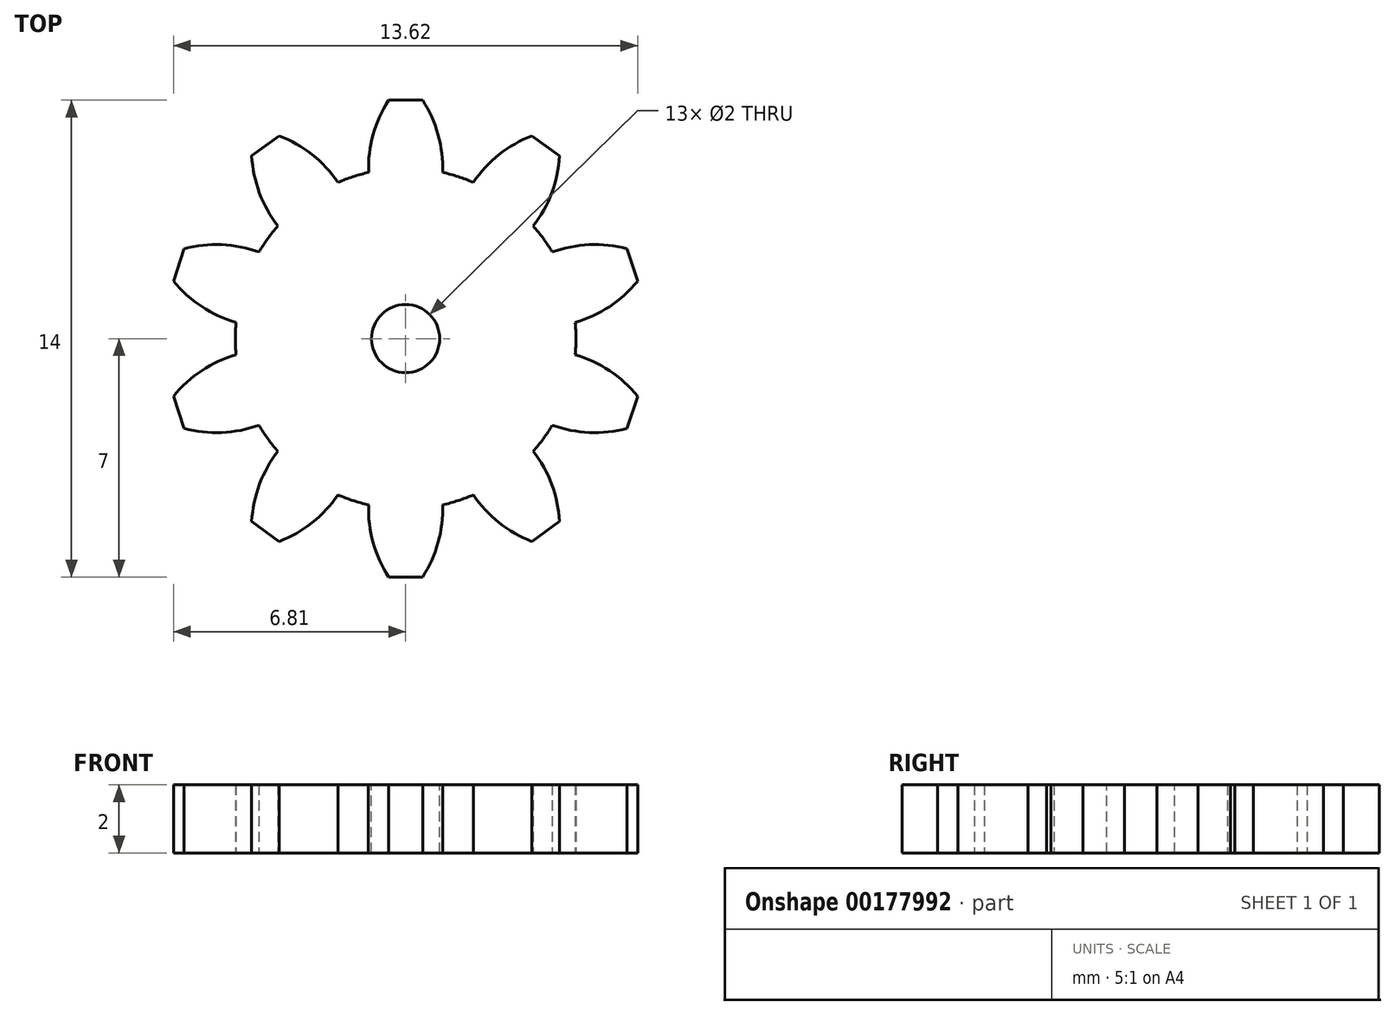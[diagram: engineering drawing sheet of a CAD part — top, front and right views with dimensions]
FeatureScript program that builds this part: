
annotation { "Feature Type Name" : "Feature", "Feature Type Description" : "" }
export const myFeature = defineFeature(function(context is Context, id is Id, definition is map)
    precondition{}
    {
        {
            var Q0;
            Q0=qCreatedBy(makeId("Top.planeOp"),FACE);
            var sketch = newSketch(context, id + "F0", { "sketchPlane" : qUnion([Q0])});
            skCircle(sketch, "E0", {"center": v(0, 0) * mm, "radius": 5 * mm});
            skLineSegment(sketch, "E1", {"start": v(0, 0) * mm, "end": v(0, 5) * mm, "construction": true});
            skLineSegment(sketch, "E2", {"start": v(0, 5) * mm, "end": v(0, 7) * mm, "construction": true});
            skLineSegment(sketch, "E3", {"start": v(0, 7) * mm, "end": v(-0.5, 7) * mm});
            skArc(sketch, "E4", {"start": v(-0.5, 7) * mm, "mid": v(-0.96, 5.98) * mm, "end": v(-1.09, 4.88) * mm});
            skLineSegment(sketch, "E5.MirrorCS", {"start": v(0, 7) * mm, "end": v(0.5, 7) * mm});
            skArc(sketch, "E6.MirrorCS", {"start": v(0.5, 7) * mm, "mid": v(0.96, 5.98) * mm, "end": v(1.09, 4.88) * mm});
            skArc(sketch, "E7.1.0", {"start": v(-4.52, 5.37) * mm, "mid": v(-4.3, 4.28) * mm, "end": v(-3.75, 3.3) * mm});
            skLineSegment(sketch, "E7.1.1", {"start": v(-4.11, 5.66) * mm, "end": v(-4.52, 5.37) * mm});
            skLineSegment(sketch, "E7.1.2", {"start": v(-4.11, 5.66) * mm, "end": v(-3.7, 5.96) * mm});
            skArc(sketch, "E7.1.3", {"start": v(-3.7, 5.96) * mm, "mid": v(-2.75, 5.4) * mm, "end": v(-1.99, 4.59) * mm});
            skArc(sketch, "E7.2.0", {"start": v(-6.81, 1.69) * mm, "mid": v(-5.99, 0.94) * mm, "end": v(-4.98, 0.47) * mm});
            skLineSegment(sketch, "E7.2.1", {"start": v(-6.66, 2.16) * mm, "end": v(-6.81, 1.69) * mm});
            skLineSegment(sketch, "E7.2.2", {"start": v(-6.66, 2.16) * mm, "end": v(-6.5, 2.64) * mm});
            skArc(sketch, "E7.2.3", {"start": v(-6.5, 2.64) * mm, "mid": v(-5.4, 2.76) * mm, "end": v(-4.3, 2.54) * mm});
            skArc(sketch, "E7.3.0", {"start": v(-6.5, -2.64) * mm, "mid": v(-5.4, -2.76) * mm, "end": v(-4.3, -2.54) * mm});
            skLineSegment(sketch, "E7.3.1", {"start": v(-6.66, -2.16) * mm, "end": v(-6.5, -2.64) * mm});
            skLineSegment(sketch, "E7.3.2", {"start": v(-6.66, -2.16) * mm, "end": v(-6.81, -1.69) * mm});
            skArc(sketch, "E7.3.3", {"start": v(-6.81, -1.69) * mm, "mid": v(-5.99, -0.94) * mm, "end": v(-4.98, -0.47) * mm});
            skArc(sketch, "E7.4.0", {"start": v(-3.7, -5.96) * mm, "mid": v(-2.75, -5.4) * mm, "end": v(-1.99, -4.59) * mm});
            skLineSegment(sketch, "E7.4.1", {"start": v(-4.11, -5.66) * mm, "end": v(-3.7, -5.96) * mm});
            skLineSegment(sketch, "E7.4.2", {"start": v(-4.11, -5.66) * mm, "end": v(-4.52, -5.37) * mm});
            skArc(sketch, "E7.4.3", {"start": v(-4.52, -5.37) * mm, "mid": v(-4.3, -4.28) * mm, "end": v(-3.75, -3.3) * mm});
            skArc(sketch, "E7.5.0", {"start": v(0.5, -7) * mm, "mid": v(0.96, -5.98) * mm, "end": v(1.09, -4.88) * mm});
            skLineSegment(sketch, "E7.5.1", {"start": v(0, -7) * mm, "end": v(0.5, -7) * mm});
            skLineSegment(sketch, "E7.5.2", {"start": v(0, -7) * mm, "end": v(-0.5, -7) * mm});
            skArc(sketch, "E7.5.3", {"start": v(-0.5, -7) * mm, "mid": v(-0.96, -5.98) * mm, "end": v(-1.09, -4.88) * mm});
            skArc(sketch, "E7.6.0", {"start": v(4.52, -5.37) * mm, "mid": v(4.3, -4.28) * mm, "end": v(3.75, -3.3) * mm});
            skLineSegment(sketch, "E7.6.1", {"start": v(4.11, -5.66) * mm, "end": v(4.52, -5.37) * mm});
            skLineSegment(sketch, "E7.6.2", {"start": v(4.11, -5.66) * mm, "end": v(3.7, -5.96) * mm});
            skArc(sketch, "E7.6.3", {"start": v(3.7, -5.96) * mm, "mid": v(2.75, -5.4) * mm, "end": v(1.99, -4.59) * mm});
            skArc(sketch, "E7.7.0", {"start": v(6.81, -1.69) * mm, "mid": v(5.99, -0.94) * mm, "end": v(4.98, -0.47) * mm});
            skLineSegment(sketch, "E7.7.1", {"start": v(6.66, -2.16) * mm, "end": v(6.81, -1.69) * mm});
            skLineSegment(sketch, "E7.7.2", {"start": v(6.66, -2.16) * mm, "end": v(6.5, -2.64) * mm});
            skArc(sketch, "E7.7.3", {"start": v(6.5, -2.64) * mm, "mid": v(5.4, -2.76) * mm, "end": v(4.3, -2.54) * mm});
            skArc(sketch, "E7.8.0", {"start": v(6.5, 2.64) * mm, "mid": v(5.4, 2.76) * mm, "end": v(4.3, 2.54) * mm});
            skLineSegment(sketch, "E7.8.1", {"start": v(6.66, 2.16) * mm, "end": v(6.5, 2.64) * mm});
            skLineSegment(sketch, "E7.8.2", {"start": v(6.66, 2.16) * mm, "end": v(6.81, 1.69) * mm});
            skArc(sketch, "E7.8.3", {"start": v(6.81, 1.69) * mm, "mid": v(5.99, 0.94) * mm, "end": v(4.98, 0.47) * mm});
            skArc(sketch, "E7.9.0", {"start": v(3.7, 5.96) * mm, "mid": v(2.75, 5.4) * mm, "end": v(1.99, 4.59) * mm});
            skLineSegment(sketch, "E7.9.1", {"start": v(4.11, 5.66) * mm, "end": v(3.7, 5.96) * mm});
            skLineSegment(sketch, "E7.9.2", {"start": v(4.11, 5.66) * mm, "end": v(4.52, 5.37) * mm});
            skArc(sketch, "E7.9.3", {"start": v(4.52, 5.37) * mm, "mid": v(4.3, 4.28) * mm, "end": v(3.75, 3.3) * mm});
            skSolve(sketch);
        }
        {
            var Q0;
            Q0=qSketchRegion(id+"F0",true);
            extrude(context, id + "F1", {"entities" : qUnion([Q0]), "depth" : 2 * mm});
        }
        {
            var Q0;
            Q0=makeQuery(id+"F1.opExtrude","CAP_FACE",FACE,{"disambiguationData":[OSD([sQuery(id+"F0.wireOp",EDGE,"E0"),sQuery(id+"F0.wireOp",EDGE,"E3"),sQuery(id+"F0.wireOp",EDGE,"E4"),sQuery(id+"F0.wireOp",EDGE,"E5.MirrorCS"),sQuery(id+"F0.wireOp",EDGE,"E6.MirrorCS"),sQuery(id+"F0.wireOp",EDGE,"E7.1.0"),sQuery(id+"F0.wireOp",EDGE,"E7.1.1"),sQuery(id+"F0.wireOp",EDGE,"E7.1.2"),sQuery(id+"F0.wireOp",EDGE,"E7.1.3"),sQuery(id+"F0.wireOp",EDGE,"E7.2.0"),sQuery(id+"F0.wireOp",EDGE,"E7.2.1"),sQuery(id+"F0.wireOp",EDGE,"E7.2.2"),sQuery(id+"F0.wireOp",EDGE,"E7.2.3"),sQuery(id+"F0.wireOp",EDGE,"E7.3.0"),sQuery(id+"F0.wireOp",EDGE,"E7.3.1"),sQuery(id+"F0.wireOp",EDGE,"E7.3.2"),sQuery(id+"F0.wireOp",EDGE,"E7.3.3"),sQuery(id+"F0.wireOp",EDGE,"E7.4.0"),sQuery(id+"F0.wireOp",EDGE,"E7.4.1"),sQuery(id+"F0.wireOp",EDGE,"E7.4.2"),sQuery(id+"F0.wireOp",EDGE,"E7.4.3"),sQuery(id+"F0.wireOp",EDGE,"E7.5.0"),sQuery(id+"F0.wireOp",EDGE,"E7.5.1"),sQuery(id+"F0.wireOp",EDGE,"E7.5.2"),sQuery(id+"F0.wireOp",EDGE,"E7.5.3"),sQuery(id+"F0.wireOp",EDGE,"E7.6.0"),sQuery(id+"F0.wireOp",EDGE,"E7.6.1"),sQuery(id+"F0.wireOp",EDGE,"E7.6.2"),sQuery(id+"F0.wireOp",EDGE,"E7.6.3"),sQuery(id+"F0.wireOp",EDGE,"E7.7.0"),sQuery(id+"F0.wireOp",EDGE,"E7.7.1"),sQuery(id+"F0.wireOp",EDGE,"E7.7.2"),sQuery(id+"F0.wireOp",EDGE,"E7.7.3"),sQuery(id+"F0.wireOp",EDGE,"E7.8.0"),sQuery(id+"F0.wireOp",EDGE,"E7.8.1"),sQuery(id+"F0.wireOp",EDGE,"E7.8.2"),sQuery(id+"F0.wireOp",EDGE,"E7.8.3"),sQuery(id+"F0.wireOp",EDGE,"E7.9.0"),sQuery(id+"F0.wireOp",EDGE,"E7.9.1"),sQuery(id+"F0.wireOp",EDGE,"E7.9.2"),sQuery(id+"F0.wireOp",EDGE,"E7.9.3"),sQuery(id+"F0.wireOp",EDGE,"E7.10.0"),sQuery(id+"F0.wireOp",EDGE,"E7.10.1"),sQuery(id+"F0.wireOp",EDGE,"E7.10.2"),sQuery(id+"F0.wireOp",EDGE,"E7.10.3"),sQuery(id+"F0.wireOp",EDGE,"E7.11.0"),sQuery(id+"F0.wireOp",EDGE,"E7.11.1"),sQuery(id+"F0.wireOp",EDGE,"E7.11.2"),sQuery(id+"F0.wireOp",EDGE,"E7.11.3"),sQuery(id+"F0.wireOp",EDGE,"E7.12.0"),sQuery(id+"F0.wireOp",EDGE,"E7.12.1"),sQuery(id+"F0.wireOp",EDGE,"E7.12.2"),sQuery(id+"F0.wireOp",EDGE,"E7.12.3"),sQuery(id+"F0.wireOp",EDGE,"E7.13.0"),sQuery(id+"F0.wireOp",EDGE,"E7.13.1"),sQuery(id+"F0.wireOp",EDGE,"E7.13.2"),sQuery(id+"F0.wireOp",EDGE,"E7.13.3"),sQuery(id+"F0.wireOp",EDGE,"E7.14.0"),sQuery(id+"F0.wireOp",EDGE,"E7.14.1"),sQuery(id+"F0.wireOp",EDGE,"E7.14.2"),sQuery(id+"F0.wireOp",EDGE,"E7.14.3"),sQuery(id+"F0.wireOp",EDGE,"E7.15.0"),sQuery(id+"F0.wireOp",EDGE,"E7.15.1"),sQuery(id+"F0.wireOp",EDGE,"E7.15.2"),sQuery(id+"F0.wireOp",EDGE,"E7.15.3")])],"isStart":false});
            var sketch = newSketch(context, id + "F2", { "sketchPlane" : qUnion([Q0])});
            skCircle(sketch, "E8", {"center": v(0, 0) * mm, "radius": 1 * mm});
            skSolve(sketch);
        }
        {
            var Q0;
            Q0=qSketchRegion(id+"F2",true);
            extrude(context, id + "F3", {"entities" : qUnion([Q0]), "operationType" : NewBodyOperationType.REMOVE, "endBound" : BoundingType.THROUGH_ALL, "oppositeDirection" : true, "depth" : 25 * mm});
        }
    });
